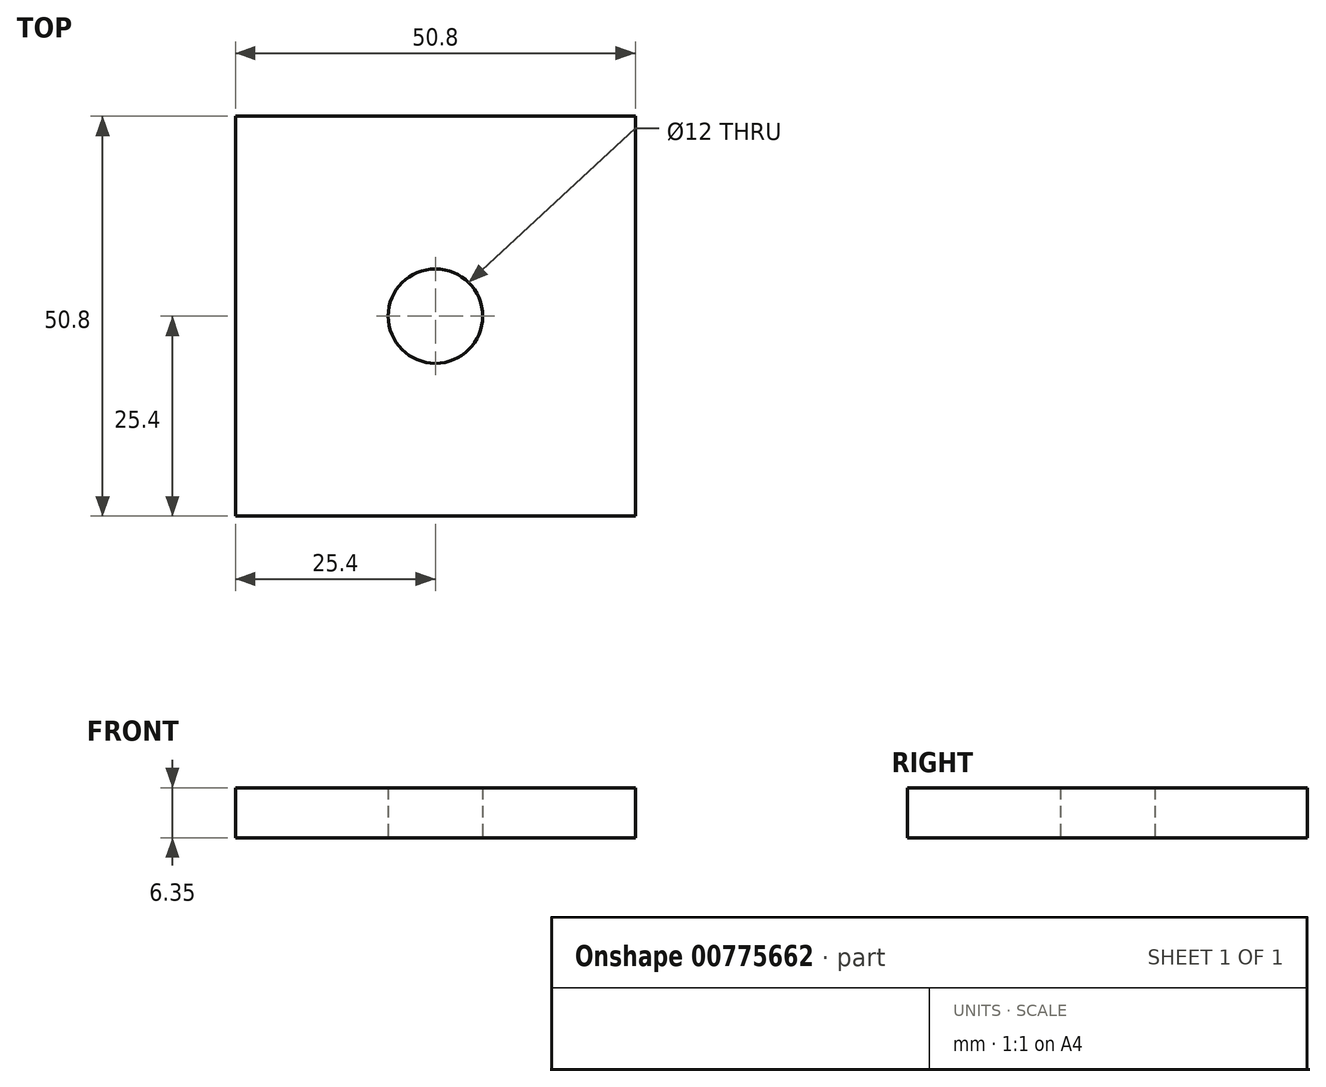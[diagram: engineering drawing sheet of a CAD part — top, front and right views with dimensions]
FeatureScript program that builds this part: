
annotation { "Feature Type Name" : "Feature", "Feature Type Description" : "" }
export const myFeature = defineFeature(function(context is Context, id is Id, definition is map)
    precondition{}
    {
        {
            var Q0;
            Q0=qCreatedBy(makeId("Top.planeOp"),FACE);
            var sketch = newSketch(context, id + "F0", { "sketchPlane" : qUnion([Q0])});
            skLineSegment(sketch, "E0.bottom", {"start": v(25.4, -25.4) * mm, "end": v(-25.4, -25.4) * mm});
            skLineSegment(sketch, "E0.top", {"start": v(25.4, 25.4) * mm, "end": v(-25.4, 25.4) * mm});
            skLineSegment(sketch, "E0.left", {"start": v(25.4, -25.4) * mm, "end": v(25.4, 25.4) * mm});
            skLineSegment(sketch, "E0.right", {"start": v(-25.4, -25.4) * mm, "end": v(-25.4, 25.4) * mm});
            skPoint(sketch, "E0.middle", {"position": v(0, 0) * mm});
            skCircle(sketch, "E1", {"center": v(0, 0) * mm, "radius": 6 * mm});
            skSolve(sketch);
        }
        {
            var Q0;
            Q0=makeQuery(id+"F0.imprint","IMPRINT",FACE,{"disambiguationData":[TD([[makeQuery(id+"F0.imprint","IMPRINT",EDGE,{"derivedFrom":sQuery(id+"F0.wireOp",EDGE,"E0.bottom")}),-1.0]])]});
            extrude(context, id + "F1", {"entities" : qUnion([Q0]), "depth" : 6.35 * mm, "offsetDistance" : 25 * mm});
        }
    });
